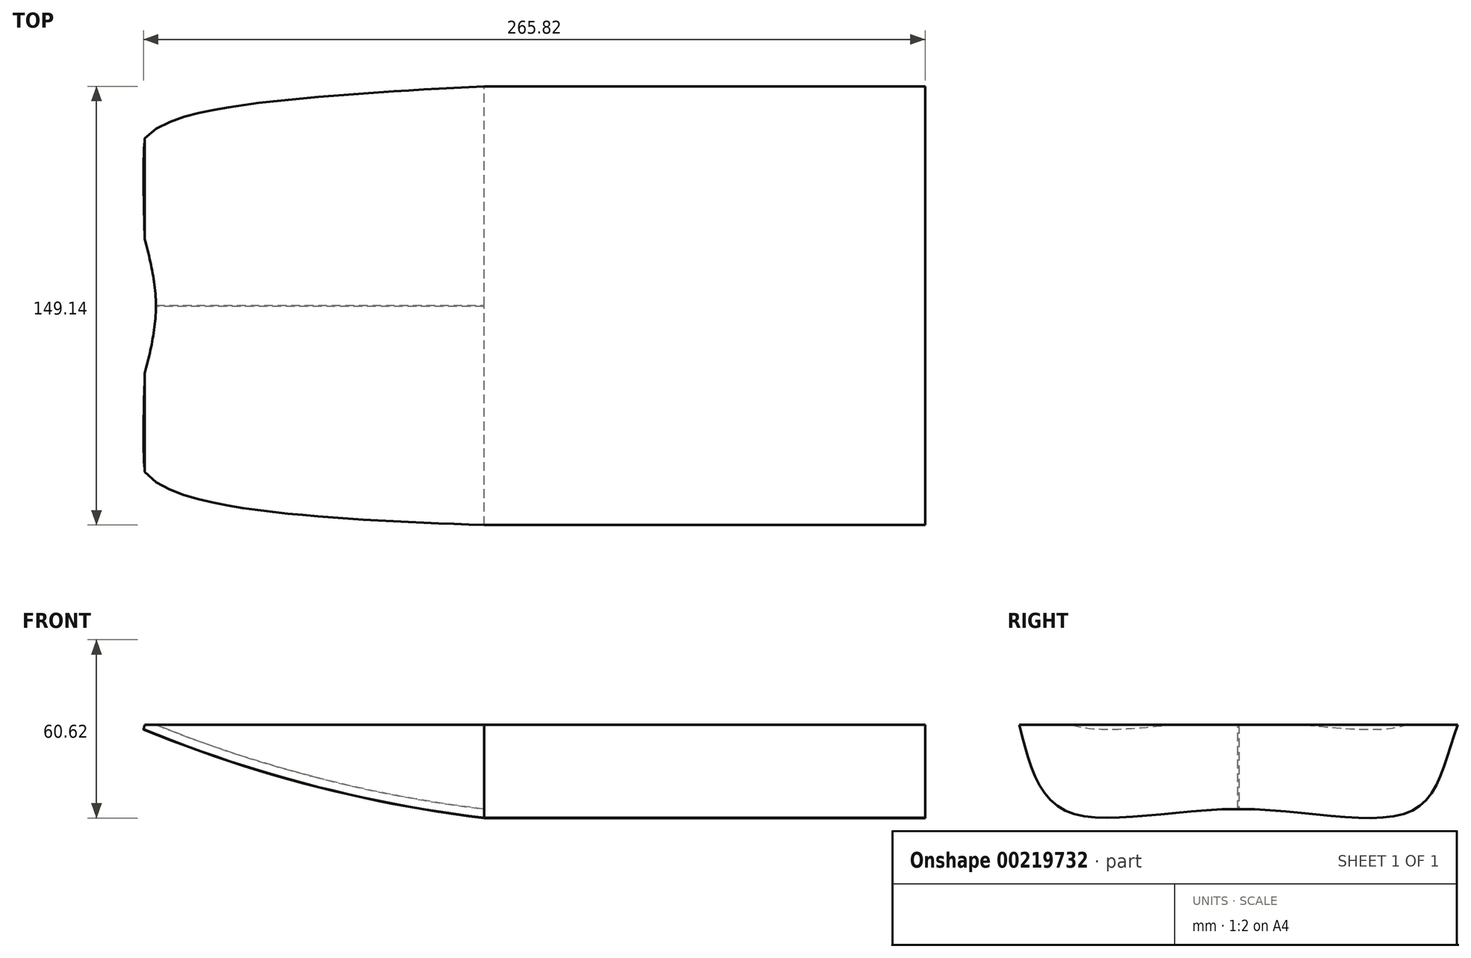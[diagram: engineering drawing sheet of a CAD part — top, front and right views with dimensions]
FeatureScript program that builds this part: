
annotation { "Feature Type Name" : "Feature", "Feature Type Description" : "" }
export const myFeature = defineFeature(function(context is Context, id is Id, definition is map)
    precondition{}
    {
        {
            var Q0;
            Q0=qCreatedBy(makeId("Front.planeOp"),FACE);
            var sketch = newSketch(context, id + "F0", { "sketchPlane" : qUnion([Q0])});
            skLineSegment(sketch, "E0.bottom", {"start": v(0, 0) * mm, "end": v(150, 0) * mm});
            skLineSegment(sketch, "E0.right", {"start": v(150, 0) * mm, "end": v(150, 30) * mm});
            skArc(sketch, "E1", {"start": v(-115, 30) * mm, "mid": v(-58.52, 11.1) * mm, "end": v(0, 0) * mm});
            skPoint(sketch, "E2.top.end.orphan", {"position": v(-115, 0) * mm});
            skSolve(sketch);
        }
        {
            var Q0;
            Q0=qCreatedBy(makeId("Right.planeOp"),FACE);
            cPlane(context, id + "F1", {"entities" : qUnion([Q0]), "cplaneType" : CPlaneType.OFFSET, "offset" : 150 * mm, "width" : 150 * mm, "height" : 150 * mm});
        }
        {
            var Q0;
            Q0=qCreatedBy(id+"F1.planeOp",FACE);
            var sketch = newSketch(context, id + "F2", { "sketchPlane" : qUnion([Q0])});
            skLineSegment(sketch, "E3.bottom", {"start": v(-75, 30) * mm, "end": v(75, 30) * mm});
            skLineSegment(sketch, "E3.top", {"start": v(-0.31, 0) * mm, "end": v(0, 0) * mm});
            skFitSpline(sketch, "E4", {"points": [v(-75, 30) * mm, v(-60, 0) * mm, v(0, 0) * mm, v(60, 0) * mm, v(75, 30) * mm], "startDerivative": vector(43.02, -173.66) * mm, "endDerivative": vector(65.03, 169.84) * mm});
            skPoint(sketch, "E5.orphan", {"position": v(-75, 0) * mm});
            skPoint(sketch, "E3.right.end.orphan", {"position": v(75, 0) * mm});
            skSolve(sketch);
        }
        {
            var Q0;
            {var subQ0=sQuery(id+"F2.wireOp",EDGE,"E3.bottom");Q0=makeQuery(id+"F2.imprint","IMPRINT",FACE,{"disambiguationData":[TD([[makeQuery(id+"F2.imprint","IMPRINT",EDGE,{"derivedFrom":subQ0}),-1.0]])]});}
            extrude(context, id + "F3", {"entities" : qUnion([Q0]), "oppositeDirection" : true, "depth" : 150 * mm});
        }
        {
            var Q0;
            Q0=makeQuery(id+"F3.opExtrude","CAP_FACE",FACE,{"disambiguationData":[OSD([sQuery(id+"F2.wireOp",EDGE,"E3.bottom"),sQuery(id+"F2.wireOp",EDGE,"E4")])],"isStart":false});
            var Q1;
            Q1 = qSketchRegion(id + "F0", true);
            var Q2;
            Q2=sQuery(id+"F0.wireOp",EDGE,"E1");
            sweep(context, id + "F4", {"operationType" : NewBodyOperationType.ADD, "profiles" : qUnion([Q0, Q1]), "path" : qUnion([Q2])});
        }
        {
            var Q0;
            Q0=qCreatedBy(makeId("Front.planeOp"),FACE);
            var sketch = newSketch(context, id + "F5", { "sketchPlane" : qUnion([Q0])});
            skLineSegment(sketch, "E6.bottom", {"start": v(154.83, 28.62) * mm, "end": v(-132.64, 28.62) * mm});
            skLineSegment(sketch, "E6.top", {"start": v(154.83, 68.12) * mm, "end": v(-132.64, 68.12) * mm});
            skLineSegment(sketch, "E6.left", {"start": v(154.83, 28.62) * mm, "end": v(154.83, 68.12) * mm});
            skLineSegment(sketch, "E6.right", {"start": v(-132.64, 28.62) * mm, "end": v(-132.64, 68.12) * mm});
            skSolve(sketch);
        }
        {
            var Q0;
            Q0 = qSketchRegion(id + "F5", true);
            extrude(context, id + "F6", {"entities" : qUnion([Q0]), "operationType" : NewBodyOperationType.REMOVE, "endBound" : BoundingType.SYMMETRIC, "oppositeDirection" : true, "depth" : 200 * mm});
        }
    });
